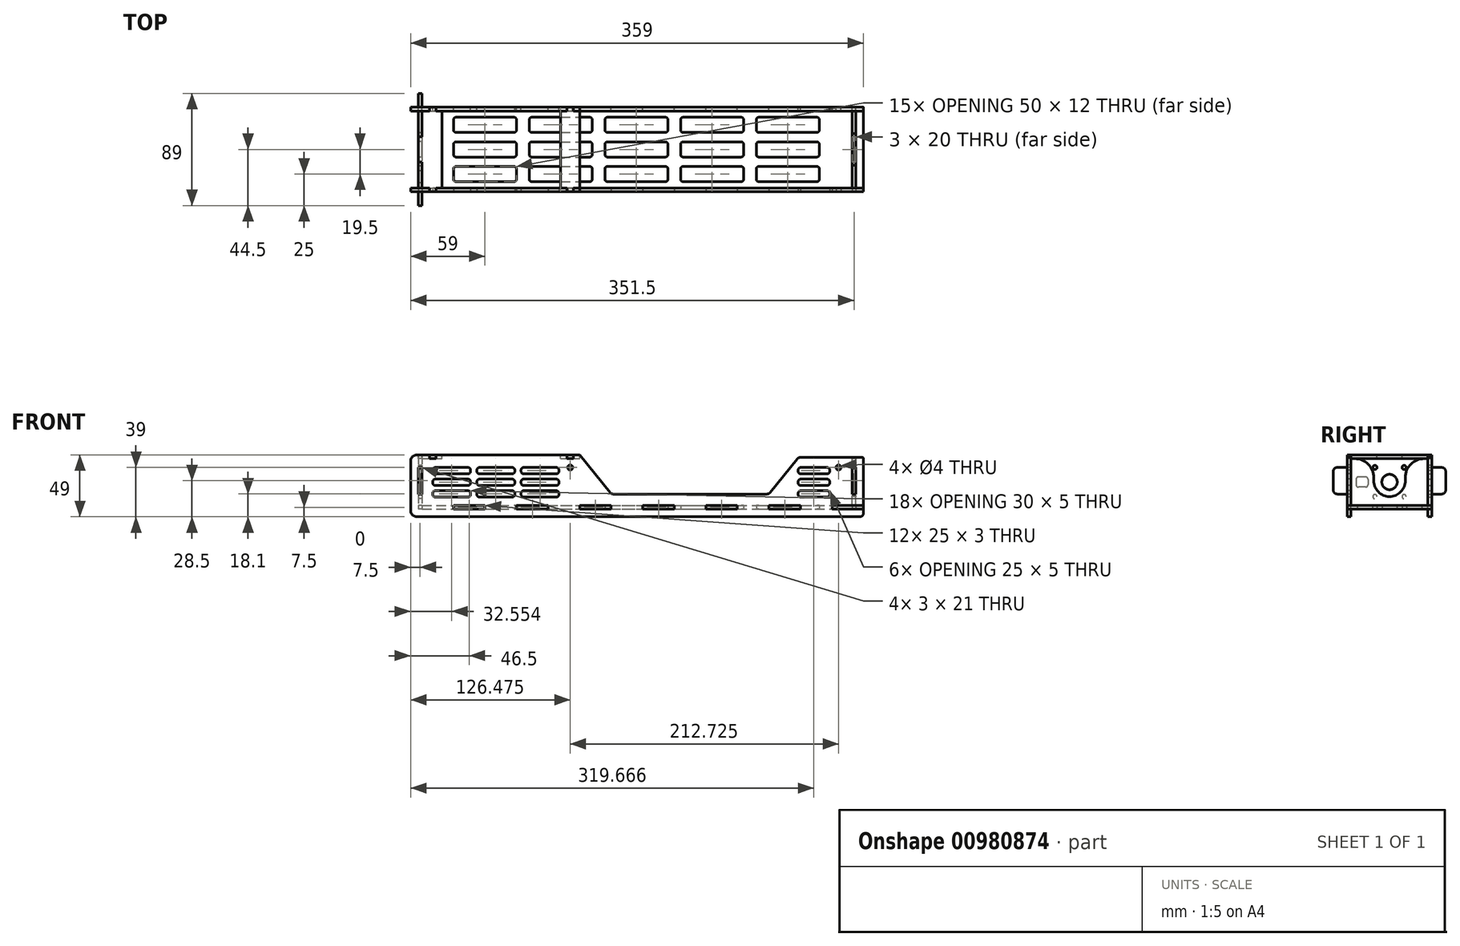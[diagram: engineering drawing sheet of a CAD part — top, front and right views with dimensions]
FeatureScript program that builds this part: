
annotation { "Feature Type Name" : "Feature", "Feature Type Description" : "" }
export const myFeature = defineFeature(function(context is Context, id is Id, definition is map)
    precondition{}
    {
        {
            assignVariable(context, id + "F0", {"variableType" : VariableType.LENGTH, "name" : "T", "lengthValue" : 3 * mm});
        }
        {
            var Q0;
            Q0=qCreatedBy(makeId("Top.planeOp"),FACE);
            var sketch = newSketch(context, id + "F1", { "sketchPlane" : qUnion([Q0])});
            skLineSegment(sketch, "E0", {"start": v(0, 0) * mm, "end": v(0, 33.5) * mm});
            skLineSegment(sketch, "E1", {"start": v(25, 33.5) * mm, "end": v(50, 33.5) * mm});
            skLineSegment(sketch, "E2", {"start": v(350, 33.5) * mm, "end": v(350, 0) * mm});
            skLineSegment(sketch, "E3", {"start": v(0, 30.5) * mm, "end": v(350, 30.5) * mm});
            skLineSegment(sketch, "E4", {"start": v(25, 33.5) * mm, "end": v(25, 30.5) * mm});
            skLineSegment(sketch, "E5.1.0.0", {"start": v(50, 33.5) * mm, "end": v(50, 30.5) * mm});
            skLineSegment(sketch, "E5.2.0.0", {"start": v(75, 33.5) * mm, "end": v(75, 30.5) * mm});
            skLineSegment(sketch, "E5.3.0.0", {"start": v(100, 33.5) * mm, "end": v(100, 30.5) * mm});
            skLineSegment(sketch, "E5.4.0.0", {"start": v(125, 33.5) * mm, "end": v(125, 30.5) * mm});
            skLineSegment(sketch, "E5.5.0.0", {"start": v(150, 33.5) * mm, "end": v(150, 30.5) * mm});
            skLineSegment(sketch, "E5.6.0.0", {"start": v(175, 33.5) * mm, "end": v(175, 30.5) * mm});
            skLineSegment(sketch, "E5.7.0.0", {"start": v(200, 33.5) * mm, "end": v(200, 30.5) * mm});
            skLineSegment(sketch, "E5.8.0.0", {"start": v(225, 33.5) * mm, "end": v(225, 30.5) * mm});
            skLineSegment(sketch, "E5.9.0.0", {"start": v(250, 33.5) * mm, "end": v(250, 30.5) * mm});
            skLineSegment(sketch, "E5.10.0.0", {"start": v(275, 33.5) * mm, "end": v(275, 30.5) * mm});
            skLineSegment(sketch, "E5.11.0.0", {"start": v(300, 33.5) * mm, "end": v(300, 30.5) * mm});
            skLineSegment(sketch, "E5.12.0.0", {"start": v(325, 33.5) * mm, "end": v(325, 30.5) * mm});
            skLineSegment(sketch, "E5.direction1", {"start": v(25, 30.5) * mm, "end": v(50, 30.5) * mm, "construction": true});
            skLineSegment(sketch, "E6.trimOffspring", {"start": v(75, 33.5) * mm, "end": v(100, 33.5) * mm});
            skLineSegment(sketch, "E7.trimOffspring", {"start": v(125, 33.5) * mm, "end": v(150, 33.5) * mm});
            skLineSegment(sketch, "E8.trimOffspring", {"start": v(175, 33.5) * mm, "end": v(200, 33.5) * mm});
            skLineSegment(sketch, "E9.trimOffspring", {"start": v(225, 33.5) * mm, "end": v(250, 33.5) * mm});
            skLineSegment(sketch, "E10.trimOffspring", {"start": v(275, 33.5) * mm, "end": v(300, 33.5) * mm});
            skLineSegment(sketch, "E11.trimOffspring", {"start": v(325, 33.5) * mm, "end": v(350, 33.5) * mm});
            skLineSegment(sketch, "E12", {"start": v(25, 0) * mm, "end": v(25, 4) * mm});
            skLineSegment(sketch, "E13", {"start": v(27, 6) * mm, "end": v(73, 6) * mm});
            skLineSegment(sketch, "E14", {"start": v(75, 4) * mm, "end": v(75, 0) * mm});
            skLineSegment(sketch, "E15", {"start": v(27, 25.5) * mm, "end": v(73, 25.5) * mm});
            skLineSegment(sketch, "E16", {"start": v(25, 23.5) * mm, "end": v(25, 15.5) * mm});
            skLineSegment(sketch, "E17", {"start": v(27, 13.5) * mm, "end": v(73, 13.5) * mm});
            skLineSegment(sketch, "E18", {"start": v(75, 15.5) * mm, "end": v(75, 23.5) * mm});
            skLineSegment(sketch, "E19.1.0.0", {"start": v(135, 15.5) * mm, "end": v(135, 23.5) * mm});
            skLineSegment(sketch, "E19.1.0.1", {"start": v(87, 13.5) * mm, "end": v(133, 13.5) * mm});
            skLineSegment(sketch, "E19.1.0.2", {"start": v(85, 23.5) * mm, "end": v(85, 15.5) * mm});
            skLineSegment(sketch, "E19.1.0.3", {"start": v(87, 25.5) * mm, "end": v(133, 25.5) * mm});
            skLineSegment(sketch, "E19.1.0.4", {"start": v(87, 6) * mm, "end": v(133, 6) * mm});
            skLineSegment(sketch, "E19.1.0.5", {"start": v(85, 0) * mm, "end": v(85, 4) * mm});
            skLineSegment(sketch, "E19.1.0.6", {"start": v(135, 4) * mm, "end": v(135, 0) * mm});
            skLineSegment(sketch, "E19.2.0.0", {"start": v(195, 15.5) * mm, "end": v(195, 23.5) * mm});
            skLineSegment(sketch, "E19.2.0.1", {"start": v(147, 13.5) * mm, "end": v(193, 13.5) * mm});
            skLineSegment(sketch, "E19.2.0.2", {"start": v(145, 23.5) * mm, "end": v(145, 15.5) * mm});
            skLineSegment(sketch, "E19.2.0.3", {"start": v(147, 25.5) * mm, "end": v(193, 25.5) * mm});
            skLineSegment(sketch, "E19.2.0.4", {"start": v(147, 6) * mm, "end": v(193, 6) * mm});
            skLineSegment(sketch, "E19.2.0.5", {"start": v(145, 0) * mm, "end": v(145, 4) * mm});
            skLineSegment(sketch, "E19.2.0.6", {"start": v(195, 4) * mm, "end": v(195, 0) * mm});
            skLineSegment(sketch, "E19.3.0.0", {"start": v(255, 15.5) * mm, "end": v(255, 23.5) * mm});
            skLineSegment(sketch, "E19.3.0.1", {"start": v(207, 13.5) * mm, "end": v(253, 13.5) * mm});
            skLineSegment(sketch, "E19.3.0.2", {"start": v(205, 23.5) * mm, "end": v(205, 15.5) * mm});
            skLineSegment(sketch, "E19.3.0.3", {"start": v(207, 25.5) * mm, "end": v(253, 25.5) * mm});
            skLineSegment(sketch, "E19.3.0.4", {"start": v(207, 6) * mm, "end": v(253, 6) * mm});
            skLineSegment(sketch, "E19.3.0.5", {"start": v(205, 0) * mm, "end": v(205, 4) * mm});
            skLineSegment(sketch, "E19.3.0.6", {"start": v(255, 4) * mm, "end": v(255, 0) * mm});
            skLineSegment(sketch, "E19.4.0.0", {"start": v(315, 15.5) * mm, "end": v(315, 23.5) * mm});
            skLineSegment(sketch, "E19.4.0.1", {"start": v(267, 13.5) * mm, "end": v(313, 13.5) * mm});
            skLineSegment(sketch, "E19.4.0.2", {"start": v(265, 23.5) * mm, "end": v(265, 15.5) * mm});
            skLineSegment(sketch, "E19.4.0.3", {"start": v(267, 25.5) * mm, "end": v(313, 25.5) * mm});
            skLineSegment(sketch, "E19.4.0.4", {"start": v(267, 6) * mm, "end": v(313, 6) * mm});
            skLineSegment(sketch, "E19.4.0.5", {"start": v(265, 0) * mm, "end": v(265, 4) * mm});
            skLineSegment(sketch, "E19.4.0.6", {"start": v(315, 4) * mm, "end": v(315, 0) * mm});
            skLineSegment(sketch, "E19.direction1", {"start": v(25, 0) * mm, "end": v(85, 0) * mm, "construction": true});
            skLineSegment(sketch, "E20.MirrorCS", {"start": v(275, -33.5) * mm, "end": v(275, -30.5) * mm});
            skLineSegment(sketch, "E21.MirrorCS", {"start": v(250, -33.5) * mm, "end": v(250, -30.5) * mm});
            skLineSegment(sketch, "E22.MirrorCS", {"start": v(300, -33.5) * mm, "end": v(300, -30.5) * mm});
            skLineSegment(sketch, "E23.MirrorCS", {"start": v(225, -33.5) * mm, "end": v(225, -30.5) * mm});
            skLineSegment(sketch, "E24.MirrorCS", {"start": v(200, -33.5) * mm, "end": v(200, -30.5) * mm});
            skLineSegment(sketch, "E25.MirrorCS", {"start": v(325, -33.5) * mm, "end": v(325, -30.5) * mm});
            skLineSegment(sketch, "E26.MirrorCS", {"start": v(175, -33.5) * mm, "end": v(175, -30.5) * mm});
            skLineSegment(sketch, "E27.MirrorCS", {"start": v(85, -23.5) * mm, "end": v(85, -15.5) * mm});
            skLineSegment(sketch, "E28.MirrorCS", {"start": v(150, -33.5) * mm, "end": v(150, -30.5) * mm});
            skLineSegment(sketch, "E29.MirrorCS", {"start": v(125, -33.5) * mm, "end": v(125, -30.5) * mm});
            skLineSegment(sketch, "E30.MirrorCS", {"start": v(135, -15.5) * mm, "end": v(135, -23.5) * mm});
            skLineSegment(sketch, "E31.MirrorCS", {"start": v(205, -23.5) * mm, "end": v(205, -15.5) * mm});
            skLineSegment(sketch, "E32.MirrorCS", {"start": v(100, -33.5) * mm, "end": v(100, -30.5) * mm});
            skLineSegment(sketch, "E33.MirrorCS", {"start": v(85, 0) * mm, "end": v(85, -4) * mm});
            skLineSegment(sketch, "E34.MirrorCS", {"start": v(50, -33.5) * mm, "end": v(50, -30.5) * mm});
            skLineSegment(sketch, "E35.MirrorCS", {"start": v(255, -15.5) * mm, "end": v(255, -23.5) * mm});
            skLineSegment(sketch, "E36.MirrorCS", {"start": v(25, -33.5) * mm, "end": v(25, -30.5) * mm});
            skLineSegment(sketch, "E37.MirrorCS", {"start": v(265, -23.5) * mm, "end": v(265, -15.5) * mm});
            skLineSegment(sketch, "E38.MirrorCS", {"start": v(25, 0) * mm, "end": v(25, -4) * mm});
            skLineSegment(sketch, "E39.MirrorCS", {"start": v(195, -15.5) * mm, "end": v(195, -23.5) * mm});
            skLineSegment(sketch, "E40.MirrorCS", {"start": v(75, -15.5) * mm, "end": v(75, -23.5) * mm});
            skLineSegment(sketch, "E41.MirrorCS", {"start": v(25, -23.5) * mm, "end": v(25, -15.5) * mm});
            skLineSegment(sketch, "E42.MirrorCS", {"start": v(315, -15.5) * mm, "end": v(315, -23.5) * mm});
            skLineSegment(sketch, "E43.MirrorCS", {"start": v(75, -33.5) * mm, "end": v(75, -30.5) * mm});
            skLineSegment(sketch, "E44.MirrorCS", {"start": v(145, -23.5) * mm, "end": v(145, -15.5) * mm});
            skLineSegment(sketch, "E45.MirrorCS", {"start": v(205, 0) * mm, "end": v(205, -4) * mm});
            skLineSegment(sketch, "E46.MirrorCS", {"start": v(255, -4) * mm, "end": v(255, 0) * mm});
            skLineSegment(sketch, "E47.MirrorCS", {"start": v(315, -4) * mm, "end": v(315, 0) * mm});
            skLineSegment(sketch, "E48.MirrorCS", {"start": v(195, -4) * mm, "end": v(195, 0) * mm});
            skLineSegment(sketch, "E49.MirrorCS", {"start": v(135, -4) * mm, "end": v(135, 0) * mm});
            skLineSegment(sketch, "E50.MirrorCS", {"start": v(75, -4) * mm, "end": v(75, 0) * mm});
            skLineSegment(sketch, "E51.MirrorCS", {"start": v(265, 0) * mm, "end": v(265, -4) * mm});
            skLineSegment(sketch, "E52.MirrorCS", {"start": v(145, 0) * mm, "end": v(145, -4) * mm});
            skLineSegment(sketch, "E53.MirrorCS", {"start": v(87, -13.5) * mm, "end": v(133, -13.5) * mm});
            skLineSegment(sketch, "E54.MirrorCS", {"start": v(207, -25.5) * mm, "end": v(253, -25.5) * mm});
            skLineSegment(sketch, "E55.MirrorCS", {"start": v(25, -30.5) * mm, "end": v(50, -30.5) * mm, "construction": true});
            skLineSegment(sketch, "E56.MirrorCS", {"start": v(207, -6) * mm, "end": v(253, -6) * mm});
            skLineSegment(sketch, "E57.MirrorCS", {"start": v(75, -33.5) * mm, "end": v(100, -33.5) * mm});
            skLineSegment(sketch, "E58.MirrorCS", {"start": v(87, -25.5) * mm, "end": v(133, -25.5) * mm});
            skLineSegment(sketch, "E59.MirrorCS", {"start": v(125, -33.5) * mm, "end": v(150, -33.5) * mm});
            skLineSegment(sketch, "E60.MirrorCS", {"start": v(87, -6) * mm, "end": v(133, -6) * mm});
            skLineSegment(sketch, "E61.MirrorCS", {"start": v(175, -33.5) * mm, "end": v(200, -33.5) * mm});
            skLineSegment(sketch, "E62.MirrorCS", {"start": v(27, -13.5) * mm, "end": v(73, -13.5) * mm});
            skLineSegment(sketch, "E63.MirrorCS", {"start": v(147, -25.5) * mm, "end": v(193, -25.5) * mm});
            skLineSegment(sketch, "E64.MirrorCS", {"start": v(0, 0) * mm, "end": v(0, -33.5) * mm});
            skLineSegment(sketch, "E65.MirrorCS", {"start": v(225, -33.5) * mm, "end": v(250, -33.5) * mm});
            skLineSegment(sketch, "E66.MirrorCS", {"start": v(147, -13.5) * mm, "end": v(193, -13.5) * mm});
            skLineSegment(sketch, "E67.MirrorCS", {"start": v(350, -33.5) * mm, "end": v(350, 0) * mm});
            skLineSegment(sketch, "E68.MirrorCS", {"start": v(27, -6) * mm, "end": v(73, -6) * mm});
            skLineSegment(sketch, "E69.MirrorCS", {"start": v(267, -6) * mm, "end": v(313, -6) * mm});
            skLineSegment(sketch, "E70.MirrorCS", {"start": v(325, -33.5) * mm, "end": v(350, -33.5) * mm});
            skLineSegment(sketch, "E71.MirrorCS", {"start": v(25, -33.5) * mm, "end": v(50, -33.5) * mm});
            skLineSegment(sketch, "E72.MirrorCS", {"start": v(147, -6) * mm, "end": v(193, -6) * mm});
            skLineSegment(sketch, "E73.MirrorCS", {"start": v(0, -30.5) * mm, "end": v(350, -30.5) * mm});
            skLineSegment(sketch, "E74.MirrorCS", {"start": v(27, -25.5) * mm, "end": v(73, -25.5) * mm});
            skLineSegment(sketch, "E75.MirrorCS", {"start": v(207, -13.5) * mm, "end": v(253, -13.5) * mm});
            skLineSegment(sketch, "E76.MirrorCS", {"start": v(275, -33.5) * mm, "end": v(300, -33.5) * mm});
            skLineSegment(sketch, "E77.MirrorCS", {"start": v(267, -25.5) * mm, "end": v(313, -25.5) * mm});
            skLineSegment(sketch, "E78.MirrorCS", {"start": v(267, -13.5) * mm, "end": v(313, -13.5) * mm});
            skLineSegment(sketch, "E79", {"start": v(0, 10) * mm, "end": v(-3, 10) * mm});
            skLineSegment(sketch, "E80", {"start": v(-3, 10) * mm, "end": v(-3, 0) * mm});
            skLineSegment(sketch, "E81.MirrorCS", {"start": v(-3, -10) * mm, "end": v(-3, 0) * mm});
            skLineSegment(sketch, "E82.MirrorCS", {"start": v(0, -10) * mm, "end": v(-3, -10) * mm});
            skLineSegment(sketch, "E83", {"start": v(350, 0) * mm, "end": v(344, 0) * mm, "construction": true});
            skLineSegment(sketch, "E84", {"start": v(344, 0) * mm, "end": v(344, 10) * mm});
            skLineSegment(sketch, "E85", {"start": v(344, 10) * mm, "end": v(341, 10) * mm});
            skLineSegment(sketch, "E86", {"start": v(341, 10) * mm, "end": v(341, -10) * mm});
            skLineSegment(sketch, "E87", {"start": v(341, -10) * mm, "end": v(344, -10) * mm});
            skLineSegment(sketch, "E88", {"start": v(344, -10) * mm, "end": v(344, 0) * mm});
            skPoint(sketch, "E89.visualSharp", {"position": v(25, 25.5) * mm});
            skArc(sketch, "E89.filletArc", {"start": v(27, 25.5) * mm, "mid": v(25.59, 24.91) * mm, "end": v(25, 23.5) * mm});
            skPoint(sketch, "E90.visualSharp", {"position": v(25, 13.5) * mm});
            skArc(sketch, "E90.filletArc", {"start": v(25, 15.5) * mm, "mid": v(25.59, 14.09) * mm, "end": v(27, 13.5) * mm});
            skPoint(sketch, "E91.visualSharp", {"position": v(75, 13.5) * mm});
            skArc(sketch, "E91.filletArc", {"start": v(73, 13.5) * mm, "mid": v(74.41, 14.09) * mm, "end": v(75, 15.5) * mm});
            skPoint(sketch, "E92.visualSharp", {"position": v(75, 25.5) * mm});
            skArc(sketch, "E92.filletArc", {"start": v(75, 23.5) * mm, "mid": v(74.41, 24.91) * mm, "end": v(73, 25.5) * mm});
            skPoint(sketch, "E93.visualSharp", {"position": v(75, 6) * mm});
            skArc(sketch, "E93.filletArc", {"start": v(75, 4) * mm, "mid": v(74.41, 5.41) * mm, "end": v(73, 6) * mm});
            skPoint(sketch, "E94.visualSharp", {"position": v(25, 6) * mm});
            skArc(sketch, "E94.filletArc", {"start": v(27, 6) * mm, "mid": v(25.59, 5.41) * mm, "end": v(25, 4) * mm});
            skPoint(sketch, "E95.visualSharp", {"position": v(25, -6) * mm});
            skArc(sketch, "E95.filletArc", {"start": v(25, -4) * mm, "mid": v(25.59, -5.41) * mm, "end": v(27, -6) * mm});
            skPoint(sketch, "E96.visualSharp", {"position": v(75, -6) * mm});
            skArc(sketch, "E96.filletArc", {"start": v(73, -6) * mm, "mid": v(74.41, -5.41) * mm, "end": v(75, -4) * mm});
            skPoint(sketch, "E97.visualSharp", {"position": v(85, 25.5) * mm});
            skArc(sketch, "E97.filletArc", {"start": v(87, 25.5) * mm, "mid": v(85.59, 24.91) * mm, "end": v(85, 23.5) * mm});
            skPoint(sketch, "E98.visualSharp", {"position": v(135, 13.5) * mm});
            skArc(sketch, "E98.filletArc", {"start": v(133, 13.5) * mm, "mid": v(134.41, 14.09) * mm, "end": v(135, 15.5) * mm});
            skPoint(sketch, "E99.visualSharp", {"position": v(135, 25.5) * mm});
            skArc(sketch, "E99.filletArc", {"start": v(135, 23.5) * mm, "mid": v(134.41, 24.91) * mm, "end": v(133, 25.5) * mm});
            skPoint(sketch, "E100.visualSharp", {"position": v(85, 13.5) * mm});
            skArc(sketch, "E100.filletArc", {"start": v(85, 15.5) * mm, "mid": v(85.59, 14.09) * mm, "end": v(87, 13.5) * mm});
            skPoint(sketch, "E101.visualSharp", {"position": v(85, 6) * mm});
            skArc(sketch, "E101.filletArc", {"start": v(87, 6) * mm, "mid": v(85.59, 5.41) * mm, "end": v(85, 4) * mm});
            skPoint(sketch, "E102.visualSharp", {"position": v(135, -6) * mm});
            skArc(sketch, "E102.filletArc", {"start": v(133, -6) * mm, "mid": v(134.41, -5.41) * mm, "end": v(135, -4) * mm});
            skPoint(sketch, "E103.visualSharp", {"position": v(85, -6) * mm});
            skArc(sketch, "E103.filletArc", {"start": v(85, -4) * mm, "mid": v(85.59, -5.41) * mm, "end": v(87, -6) * mm});
            skPoint(sketch, "E104.visualSharp", {"position": v(135, 6) * mm});
            skArc(sketch, "E104.filletArc", {"start": v(135, 4) * mm, "mid": v(134.41, 5.41) * mm, "end": v(133, 6) * mm});
            skPoint(sketch, "E105.visualSharp", {"position": v(145, 13.5) * mm});
            skArc(sketch, "E105.filletArc", {"start": v(145, 15.5) * mm, "mid": v(145.59, 14.09) * mm, "end": v(147, 13.5) * mm});
            skPoint(sketch, "E106.visualSharp", {"position": v(145, 25.5) * mm});
            skArc(sketch, "E106.filletArc", {"start": v(147, 25.5) * mm, "mid": v(145.59, 24.91) * mm, "end": v(145, 23.5) * mm});
            skPoint(sketch, "E107.visualSharp", {"position": v(195, 25.5) * mm});
            skArc(sketch, "E107.filletArc", {"start": v(195, 23.5) * mm, "mid": v(194.41, 24.91) * mm, "end": v(193, 25.5) * mm});
            skPoint(sketch, "E108.visualSharp", {"position": v(195, 6) * mm});
            skArc(sketch, "E108.filletArc", {"start": v(195, 4) * mm, "mid": v(194.41, 5.41) * mm, "end": v(193, 6) * mm});
            skPoint(sketch, "E109.visualSharp", {"position": v(195, 13.5) * mm});
            skArc(sketch, "E109.filletArc", {"start": v(193, 13.5) * mm, "mid": v(194.41, 14.09) * mm, "end": v(195, 15.5) * mm});
            skPoint(sketch, "E110.visualSharp", {"position": v(145, -6) * mm});
            skArc(sketch, "E110.filletArc", {"start": v(145, -4) * mm, "mid": v(145.59, -5.41) * mm, "end": v(147, -6) * mm});
            skPoint(sketch, "E111.visualSharp", {"position": v(145, 6) * mm});
            skArc(sketch, "E111.filletArc", {"start": v(147, 6) * mm, "mid": v(145.59, 5.41) * mm, "end": v(145, 4) * mm});
            skPoint(sketch, "E112.visualSharp", {"position": v(195, -6) * mm});
            skArc(sketch, "E112.filletArc", {"start": v(193, -6) * mm, "mid": v(194.41, -5.41) * mm, "end": v(195, -4) * mm});
            skPoint(sketch, "E113.visualSharp", {"position": v(25, -13.5) * mm});
            skArc(sketch, "E113.filletArc", {"start": v(27, -13.5) * mm, "mid": v(25.59, -14.09) * mm, "end": v(25, -15.5) * mm});
            skPoint(sketch, "E114.visualSharp", {"position": v(75, -25.5) * mm});
            skArc(sketch, "E114.filletArc", {"start": v(73, -25.5) * mm, "mid": v(74.41, -24.91) * mm, "end": v(75, -23.5) * mm});
            skPoint(sketch, "E115.visualSharp", {"position": v(75, -13.5) * mm});
            skArc(sketch, "E115.filletArc", {"start": v(75, -15.5) * mm, "mid": v(74.41, -14.09) * mm, "end": v(73, -13.5) * mm});
            skPoint(sketch, "E116.visualSharp", {"position": v(25, -25.5) * mm});
            skArc(sketch, "E116.filletArc", {"start": v(25, -23.5) * mm, "mid": v(25.59, -24.91) * mm, "end": v(27, -25.5) * mm});
            skPoint(sketch, "E117.visualSharp", {"position": v(85, -25.5) * mm});
            skArc(sketch, "E117.filletArc", {"start": v(85, -23.5) * mm, "mid": v(85.59, -24.91) * mm, "end": v(87, -25.5) * mm});
            skPoint(sketch, "E118.visualSharp", {"position": v(85, -13.5) * mm});
            skArc(sketch, "E118.filletArc", {"start": v(87, -13.5) * mm, "mid": v(85.59, -14.09) * mm, "end": v(85, -15.5) * mm});
            skPoint(sketch, "E119.visualSharp", {"position": v(135, -13.5) * mm});
            skArc(sketch, "E119.filletArc", {"start": v(135, -15.5) * mm, "mid": v(134.41, -14.09) * mm, "end": v(133, -13.5) * mm});
            skPoint(sketch, "E120.visualSharp", {"position": v(135, -25.5) * mm});
            skArc(sketch, "E120.filletArc", {"start": v(133, -25.5) * mm, "mid": v(134.41, -24.91) * mm, "end": v(135, -23.5) * mm});
            skPoint(sketch, "E121.visualSharp", {"position": v(145, -13.5) * mm});
            skArc(sketch, "E121.filletArc", {"start": v(147, -13.5) * mm, "mid": v(145.59, -14.09) * mm, "end": v(145, -15.5) * mm});
            skPoint(sketch, "E122.visualSharp", {"position": v(145, -25.5) * mm});
            skArc(sketch, "E122.filletArc", {"start": v(145, -23.5) * mm, "mid": v(145.59, -24.91) * mm, "end": v(147, -25.5) * mm});
            skPoint(sketch, "E123.visualSharp", {"position": v(195, -25.5) * mm});
            skArc(sketch, "E123.filletArc", {"start": v(193, -25.5) * mm, "mid": v(194.41, -24.91) * mm, "end": v(195, -23.5) * mm});
            skPoint(sketch, "E124.visualSharp", {"position": v(195, -13.5) * mm});
            skArc(sketch, "E124.filletArc", {"start": v(195, -15.5) * mm, "mid": v(194.41, -14.09) * mm, "end": v(193, -13.5) * mm});
            skPoint(sketch, "E125.visualSharp", {"position": v(205, -25.5) * mm});
            skArc(sketch, "E125.filletArc", {"start": v(205, -23.5) * mm, "mid": v(205.59, -24.91) * mm, "end": v(207, -25.5) * mm});
            skPoint(sketch, "E126.visualSharp", {"position": v(205, -13.5) * mm});
            skArc(sketch, "E126.filletArc", {"start": v(207, -13.5) * mm, "mid": v(205.59, -14.09) * mm, "end": v(205, -15.5) * mm});
            skPoint(sketch, "E127.visualSharp", {"position": v(205, -6) * mm});
            skArc(sketch, "E127.filletArc", {"start": v(205, -4) * mm, "mid": v(205.59, -5.41) * mm, "end": v(207, -6) * mm});
            skPoint(sketch, "E128.visualSharp", {"position": v(205, 6) * mm});
            skArc(sketch, "E128.filletArc", {"start": v(207, 6) * mm, "mid": v(205.59, 5.41) * mm, "end": v(205, 4) * mm});
            skPoint(sketch, "E129.visualSharp", {"position": v(205, 25.5) * mm});
            skArc(sketch, "E129.filletArc", {"start": v(207, 25.5) * mm, "mid": v(205.59, 24.91) * mm, "end": v(205, 23.5) * mm});
            skPoint(sketch, "E130.visualSharp", {"position": v(205, 13.5) * mm});
            skArc(sketch, "E130.filletArc", {"start": v(205, 15.5) * mm, "mid": v(205.59, 14.09) * mm, "end": v(207, 13.5) * mm});
            skPoint(sketch, "E131.visualSharp", {"position": v(255, 25.5) * mm});
            skArc(sketch, "E131.filletArc", {"start": v(255, 23.5) * mm, "mid": v(254.41, 24.91) * mm, "end": v(253, 25.5) * mm});
            skPoint(sketch, "E132.visualSharp", {"position": v(255, 13.5) * mm});
            skArc(sketch, "E132.filletArc", {"start": v(253, 13.5) * mm, "mid": v(254.41, 14.09) * mm, "end": v(255, 15.5) * mm});
            skPoint(sketch, "E133.visualSharp", {"position": v(255, 6) * mm});
            skArc(sketch, "E133.filletArc", {"start": v(255, 4) * mm, "mid": v(254.41, 5.41) * mm, "end": v(253, 6) * mm});
            skPoint(sketch, "E134.visualSharp", {"position": v(255, -6) * mm});
            skArc(sketch, "E134.filletArc", {"start": v(253, -6) * mm, "mid": v(254.41, -5.41) * mm, "end": v(255, -4) * mm});
            skPoint(sketch, "E135.visualSharp", {"position": v(255, -25.5) * mm});
            skArc(sketch, "E135.filletArc", {"start": v(253, -25.5) * mm, "mid": v(254.41, -24.91) * mm, "end": v(255, -23.5) * mm});
            skPoint(sketch, "E136.visualSharp", {"position": v(255, -13.5) * mm});
            skArc(sketch, "E136.filletArc", {"start": v(255, -15.5) * mm, "mid": v(254.41, -14.09) * mm, "end": v(253, -13.5) * mm});
            skPoint(sketch, "E137.visualSharp", {"position": v(265, -25.5) * mm});
            skArc(sketch, "E137.filletArc", {"start": v(265, -23.5) * mm, "mid": v(265.59, -24.91) * mm, "end": v(267, -25.5) * mm});
            skPoint(sketch, "E138.visualSharp", {"position": v(265, -13.5) * mm});
            skArc(sketch, "E138.filletArc", {"start": v(267, -13.5) * mm, "mid": v(265.59, -14.09) * mm, "end": v(265, -15.5) * mm});
            skPoint(sketch, "E139.visualSharp", {"position": v(265, -6) * mm});
            skArc(sketch, "E139.filletArc", {"start": v(265, -4) * mm, "mid": v(265.59, -5.41) * mm, "end": v(267, -6) * mm});
            skPoint(sketch, "E140.visualSharp", {"position": v(265, 6) * mm});
            skArc(sketch, "E140.filletArc", {"start": v(267, 6) * mm, "mid": v(265.59, 5.41) * mm, "end": v(265, 4) * mm});
            skPoint(sketch, "E141.visualSharp", {"position": v(265, 13.5) * mm});
            skArc(sketch, "E141.filletArc", {"start": v(265, 15.5) * mm, "mid": v(265.59, 14.09) * mm, "end": v(267, 13.5) * mm});
            skPoint(sketch, "E142.visualSharp", {"position": v(265, 25.5) * mm});
            skArc(sketch, "E142.filletArc", {"start": v(267, 25.5) * mm, "mid": v(265.59, 24.91) * mm, "end": v(265, 23.5) * mm});
            skPoint(sketch, "E143.visualSharp", {"position": v(315, 25.5) * mm});
            skArc(sketch, "E143.filletArc", {"start": v(315, 23.5) * mm, "mid": v(314.41, 24.91) * mm, "end": v(313, 25.5) * mm});
            skPoint(sketch, "E144.visualSharp", {"position": v(315, 13.5) * mm});
            skArc(sketch, "E144.filletArc", {"start": v(313, 13.5) * mm, "mid": v(314.41, 14.09) * mm, "end": v(315, 15.5) * mm});
            skPoint(sketch, "E145.visualSharp", {"position": v(315, -6) * mm});
            skArc(sketch, "E145.filletArc", {"start": v(313, -6) * mm, "mid": v(314.41, -5.41) * mm, "end": v(315, -4) * mm});
            skPoint(sketch, "E146.visualSharp", {"position": v(315, 6) * mm});
            skArc(sketch, "E146.filletArc", {"start": v(315, 4) * mm, "mid": v(314.41, 5.41) * mm, "end": v(313, 6) * mm});
            skPoint(sketch, "E147.visualSharp", {"position": v(315, -13.5) * mm});
            skArc(sketch, "E147.filletArc", {"start": v(315, -15.5) * mm, "mid": v(314.41, -14.09) * mm, "end": v(313, -13.5) * mm});
            skPoint(sketch, "E148.visualSharp", {"position": v(315, -25.5) * mm});
            skArc(sketch, "E148.filletArc", {"start": v(313, -25.5) * mm, "mid": v(314.41, -24.91) * mm, "end": v(315, -23.5) * mm});
            skSolve(sketch);
        }
        {
            var Q0;
            Q0=makeQuery(id+"F1.imprint","IMPRINT",FACE,{"disambiguationData":[TD([[makeQuery(id+"F1.imprint","IMPRINT",EDGE,{"derivedFrom":sQuery(id+"F1.wireOp",EDGE,"E12")}),1.0]])]});
            var Q1;
            Q1=makeQuery(id+"F1.imprint","IMPRINT",FACE,{"disambiguationData":[TD([[makeQuery(id+"F1.imprint","IMPRINT",EDGE,{"derivedFrom":sQuery(id+"F1.wireOp",EDGE,"E1")}),-1.0]])]});
            var Q2;
            {var subQ0=sQuery(id+"F1.wireOp",EDGE,"E5.2.0.0");Q2=makeQuery(id+"F1.imprint","IMPRINT",FACE,{"disambiguationData":[TD([[makeQuery(id+"F1.imprint","IMPRINT",EDGE,{"derivedFrom":subQ0}),1.0]])]});}
            var Q3;
            {var subQ0=sQuery(id+"F1.wireOp",EDGE,"E5.4.0.0");Q3=makeQuery(id+"F1.imprint","IMPRINT",FACE,{"disambiguationData":[TD([[makeQuery(id+"F1.imprint","IMPRINT",EDGE,{"derivedFrom":subQ0}),1.0]])]});}
            var Q4;
            {var subQ0=sQuery(id+"F1.wireOp",EDGE,"E5.6.0.0");Q4=makeQuery(id+"F1.imprint","IMPRINT",FACE,{"disambiguationData":[TD([[makeQuery(id+"F1.imprint","IMPRINT",EDGE,{"derivedFrom":subQ0}),1.0]])]});}
            var Q5;
            {var subQ0=sQuery(id+"F1.wireOp",EDGE,"E5.8.0.0");Q5=makeQuery(id+"F1.imprint","IMPRINT",FACE,{"disambiguationData":[TD([[makeQuery(id+"F1.imprint","IMPRINT",EDGE,{"derivedFrom":subQ0}),1.0]])]});}
            var Q6;
            {var subQ0=sQuery(id+"F1.wireOp",EDGE,"E34.MirrorCS");Q6=makeQuery(id+"F1.imprint","IMPRINT",FACE,{"disambiguationData":[TD([[makeQuery(id+"F1.imprint","IMPRINT",EDGE,{"derivedFrom":subQ0}),1.0]])]});}
            var Q7;
            {var subQ0=sQuery(id+"F1.wireOp",EDGE,"E32.MirrorCS");Q7=makeQuery(id+"F1.imprint","IMPRINT",FACE,{"disambiguationData":[TD([[makeQuery(id+"F1.imprint","IMPRINT",EDGE,{"derivedFrom":subQ0}),1.0]])]});}
            var Q8;
            {var subQ0=sQuery(id+"F1.wireOp",EDGE,"E28.MirrorCS");Q8=makeQuery(id+"F1.imprint","IMPRINT",FACE,{"disambiguationData":[TD([[makeQuery(id+"F1.imprint","IMPRINT",EDGE,{"derivedFrom":subQ0}),1.0]])]});}
            var Q9;
            {var subQ0=sQuery(id+"F1.wireOp",EDGE,"E24.MirrorCS");Q9=makeQuery(id+"F1.imprint","IMPRINT",FACE,{"disambiguationData":[TD([[makeQuery(id+"F1.imprint","IMPRINT",EDGE,{"derivedFrom":subQ0}),1.0]])]});}
            var Q10;
            {var subQ0=sQuery(id+"F1.wireOp",EDGE,"E21.MirrorCS");Q10=makeQuery(id+"F1.imprint","IMPRINT",FACE,{"disambiguationData":[TD([[makeQuery(id+"F1.imprint","IMPRINT",EDGE,{"derivedFrom":subQ0}),1.0]])]});}
            var Q11;
            {var subQ0=sQuery(id+"F1.wireOp",EDGE,"E5.10.0.0");Q11=makeQuery(id+"F1.imprint","IMPRINT",FACE,{"disambiguationData":[TD([[makeQuery(id+"F1.imprint","IMPRINT",EDGE,{"derivedFrom":subQ0}),1.0]])]});}
            var Q12;
            {var subQ4=sQuery(id+"F1.wireOp",EDGE,"E5.12.0.0");Q12=makeQuery(id+"F1.imprint","IMPRINT",FACE,{"disambiguationData":[TD([[makeQuery(id+"F1.imprint","IMPRINT",EDGE,{"derivedFrom":subQ4}),1.0]])]});}
            var Q13;
            {var subQ0=sQuery(id+"F1.wireOp",EDGE,"E20.MirrorCS");Q13=makeQuery(id+"F1.imprint","IMPRINT",FACE,{"disambiguationData":[TD([[makeQuery(id+"F1.imprint","IMPRINT",EDGE,{"derivedFrom":subQ0}),-1.0]])]});}
            var Q14;
            {var subQ0=sQuery(id+"F1.wireOp",EDGE,"E25.MirrorCS");Q14=makeQuery(id+"F1.imprint","IMPRINT",FACE,{"disambiguationData":[TD([[makeQuery(id+"F1.imprint","IMPRINT",EDGE,{"derivedFrom":subQ0}),-1.0]])]});}
            var Q15;
            {var subQ0=sQuery(id+"F1.wireOp",EDGE,"E79");Q15=makeQuery(id+"F1.imprint","IMPRINT",FACE,{"disambiguationData":[TD([[makeQuery(id+"F1.imprint","IMPRINT",EDGE,{"derivedFrom":subQ0}),1.0]])]});}
            extrude(context, id + "F2", {"entities" : qUnion([Q0, Q1, Q2, Q3, Q4, Q5, Q6, Q7, Q8, Q9, Q10, Q11, Q12, Q13, Q14, Q15]), "depth" : getVariable(context, 'T'), "offsetDistance" : 25 * mm});
        }
        {
            var Q0;
            Q0=makeQuery(id+"F2.opExtrude","SWEPT_FACE",FACE,{"disambiguationData":[OSD([sQuery(id+"F1.wireOp",EDGE,"E71.MirrorCS")])]});
            var sketch = newSketch(context, id + "F3", { "sketchPlane" : qUnion([Q0])});
            skLineSegment(sketch, "E149.0.1", {"start": v(25, 0) * mm, "end": v(25, 3) * mm});
            skLineSegment(sketch, "E149.0.3", {"start": v(0, 3) * mm, "end": v(0, 0) * mm});
            skLineSegment(sketch, "E150.0.0", {"start": v(25, 0) * mm, "end": v(50, 0) * mm});
            skLineSegment(sketch, "E150.0.1", {"start": v(50, 0) * mm, "end": v(50, 3) * mm});
            skLineSegment(sketch, "E150.0.2", {"start": v(50, 3) * mm, "end": v(25, 3) * mm});
            skLineSegment(sketch, "E150.0.3", {"start": v(25, 3) * mm, "end": v(25, 0) * mm});
            skLineSegment(sketch, "E151.0.1", {"start": v(75, 0) * mm, "end": v(75, 3) * mm});
            skLineSegment(sketch, "E151.0.3", {"start": v(50, 3) * mm, "end": v(50, 0) * mm});
            skLineSegment(sketch, "E152.0.0", {"start": v(75, 0) * mm, "end": v(100, 0) * mm});
            skLineSegment(sketch, "E152.0.1", {"start": v(100, 0) * mm, "end": v(100, 3) * mm});
            skLineSegment(sketch, "E152.0.2", {"start": v(100, 3) * mm, "end": v(75, 3) * mm});
            skLineSegment(sketch, "E152.0.3", {"start": v(75, 3) * mm, "end": v(75, 0) * mm});
            skLineSegment(sketch, "E153.0.1", {"start": v(125, 0) * mm, "end": v(125, 3) * mm});
            skLineSegment(sketch, "E153.0.3", {"start": v(100, 3) * mm, "end": v(100, 0) * mm});
            skLineSegment(sketch, "E154.0.0", {"start": v(125, 0) * mm, "end": v(150, 0) * mm});
            skLineSegment(sketch, "E154.0.1", {"start": v(150, 0) * mm, "end": v(150, 3) * mm});
            skLineSegment(sketch, "E154.0.2", {"start": v(150, 3) * mm, "end": v(125, 3) * mm});
            skLineSegment(sketch, "E154.0.3", {"start": v(125, 3) * mm, "end": v(125, 0) * mm});
            skLineSegment(sketch, "E155.0.1", {"start": v(175, 0) * mm, "end": v(175, 3) * mm});
            skLineSegment(sketch, "E155.0.3", {"start": v(150, 3) * mm, "end": v(150, 0) * mm});
            skLineSegment(sketch, "E156.0.0", {"start": v(175, 0) * mm, "end": v(200, 0) * mm});
            skLineSegment(sketch, "E156.0.1", {"start": v(200, 0) * mm, "end": v(200, 3) * mm});
            skLineSegment(sketch, "E156.0.2", {"start": v(200, 3) * mm, "end": v(175, 3) * mm});
            skLineSegment(sketch, "E156.0.3", {"start": v(175, 3) * mm, "end": v(175, 0) * mm});
            skLineSegment(sketch, "E157.0.1", {"start": v(225, 0) * mm, "end": v(225, 3) * mm});
            skLineSegment(sketch, "E157.0.3", {"start": v(200, 3) * mm, "end": v(200, 0) * mm});
            skLineSegment(sketch, "E158.0.0", {"start": v(225, 0) * mm, "end": v(250, 0) * mm});
            skLineSegment(sketch, "E158.0.1", {"start": v(250, 0) * mm, "end": v(250, 3) * mm});
            skLineSegment(sketch, "E158.0.2", {"start": v(250, 3) * mm, "end": v(225, 3) * mm});
            skLineSegment(sketch, "E158.0.3", {"start": v(225, 3) * mm, "end": v(225, 0) * mm});
            skLineSegment(sketch, "E159.0.1", {"start": v(275, 0) * mm, "end": v(275, 3) * mm});
            skLineSegment(sketch, "E159.0.3", {"start": v(250, 3) * mm, "end": v(250, 0) * mm});
            skLineSegment(sketch, "E160.0.0", {"start": v(275, 0) * mm, "end": v(300, 0) * mm});
            skLineSegment(sketch, "E160.0.1", {"start": v(300, 0) * mm, "end": v(300, 3) * mm});
            skLineSegment(sketch, "E160.0.2", {"start": v(300, 3) * mm, "end": v(275, 3) * mm});
            skLineSegment(sketch, "E160.0.3", {"start": v(275, 3) * mm, "end": v(275, 0) * mm});
            skLineSegment(sketch, "E161.0.1", {"start": v(325, 0) * mm, "end": v(325, 3) * mm});
            skLineSegment(sketch, "E161.0.3", {"start": v(300, 3) * mm, "end": v(300, 0) * mm});
            skLineSegment(sketch, "E162.0.0", {"start": v(325, 0) * mm, "end": v(350, 0) * mm});
            skLineSegment(sketch, "E162.0.2", {"start": v(350, 3) * mm, "end": v(325, 3) * mm});
            skLineSegment(sketch, "E162.0.3", {"start": v(325, 3) * mm, "end": v(325, 0) * mm});
            skLineSegment(sketch, "E163", {"start": v(0, 0) * mm, "end": v(0, -6) * mm});
            skLineSegment(sketch, "E164", {"start": v(0, -6) * mm, "end": v(347, -6) * mm});
            skLineSegment(sketch, "E165", {"start": v(350, -3) * mm, "end": v(350, 0) * mm});
            skLineSegment(sketch, "E166", {"start": v(0, 3) * mm, "end": v(0, 12) * mm, "construction": true});
            skLineSegment(sketch, "E167", {"start": v(0, 43) * mm, "end": v(6, 43) * mm});
            skLineSegment(sketch, "E168", {"start": v(350, 40) * mm, "end": v(350, 3) * mm});
            skLineSegment(sketch, "E169", {"start": v(0, 12) * mm, "end": v(150, 12) * mm, "construction": true});
            skPoint(sketch, "E169.endSnap0", {"position": v(350, 23) * mm});
            skLineSegment(sketch, "E170", {"start": v(117.48, 43) * mm, "end": v(117.48, 12) * mm, "construction": true});
            skLineSegment(sketch, "E171", {"start": v(330.2, 43) * mm, "end": v(330.2, 12) * mm, "construction": true});
            skLineSegment(sketch, "E172", {"start": v(125, 43) * mm, "end": v(149.1, 13.12) * mm});
            skLineSegment(sketch, "E173", {"start": v(297.49, 39.88) * mm, "end": v(275.9, 13.12) * mm});
            skLineSegment(sketch, "E174", {"start": v(0, 33) * mm, "end": v(8.55, 33) * mm, "construction": true});
            skCircle(sketch, "E175", {"center": v(117.48, 33) * mm, "radius": 2 * mm});
            skCircle(sketch, "E176", {"center": v(330.2, 33) * mm, "radius": 2 * mm});
            skLineSegment(sketch, "E177", {"start": v(6, 43) * mm, "end": v(6, 40) * mm});
            skLineSegment(sketch, "E178", {"start": v(6, 40) * mm, "end": v(11, 40) * mm});
            skLineSegment(sketch, "E179", {"start": v(11, 40) * mm, "end": v(11, 43) * mm});
            skLineSegment(sketch, "E180.trimOffspring", {"start": v(11, 43) * mm, "end": v(115, 43) * mm});
            skLineSegment(sketch, "E181", {"start": v(0, 33) * mm, "end": v(-3, 33) * mm});
            skLineSegment(sketch, "E182", {"start": v(-3, 33) * mm, "end": v(-3, 12) * mm});
            skLineSegment(sketch, "E183", {"start": v(-3, 12) * mm, "end": v(0, 12) * mm});
            skLineSegment(sketch, "E184", {"start": v(0, -6) * mm, "end": v(-4, -6) * mm});
            skLineSegment(sketch, "E185", {"start": v(-9, -1) * mm, "end": v(-9, 38) * mm});
            skLineSegment(sketch, "E186", {"start": v(-4, 43) * mm, "end": v(0, 43) * mm});
            skPoint(sketch, "E187.visualSharp", {"position": v(-9, 43) * mm});
            skArc(sketch, "E187.filletArc", {"start": v(-4, 43) * mm, "mid": v(-7.54, 41.54) * mm, "end": v(-9, 38) * mm});
            skPoint(sketch, "E188.visualSharp", {"position": v(-9, -6) * mm});
            skArc(sketch, "E188.filletArc", {"start": v(-9, -1) * mm, "mid": v(-7.54, -4.54) * mm, "end": v(-4, -6) * mm});
            skLineSegment(sketch, "E189", {"start": v(125, 43) * mm, "end": v(120, 43) * mm});
            skLineSegment(sketch, "E190", {"start": v(120, 43) * mm, "end": v(120, 40) * mm});
            skLineSegment(sketch, "E191", {"start": v(120, 40) * mm, "end": v(115, 40) * mm});
            skLineSegment(sketch, "E192", {"start": v(115, 40) * mm, "end": v(115, 43) * mm});
            skLineSegment(sketch, "E193.trimOffspring", {"start": v(120, 43) * mm, "end": v(125, 43) * mm});
            skLineSegment(sketch, "E194", {"start": v(344, 33) * mm, "end": v(344, 12) * mm});
            skLineSegment(sketch, "E195", {"start": v(344, 12) * mm, "end": v(341, 12) * mm});
            skLineSegment(sketch, "E196", {"start": v(341, 12) * mm, "end": v(341, 33) * mm});
            skLineSegment(sketch, "E197", {"start": v(341, 33) * mm, "end": v(344, 33) * mm});
            skPoint(sketch, "E198.start.orphan", {"position": v(350, 33) * mm});
            skPoint(sketch, "E199.orphan", {"position": v(350, 12) * mm});
            skLineSegment(sketch, "E200.trimOffspring", {"start": v(275, 12) * mm, "end": v(344, 12) * mm, "construction": true});
            skLineSegment(sketch, "E201", {"start": v(151.43, 12) * mm, "end": v(273.57, 12) * mm});
            skLineSegment(sketch, "E202.trimOffspring", {"start": v(0, 33) * mm, "end": v(0, 43) * mm, "construction": true});
            skLineSegment(sketch, "E203", {"start": v(0, 33) * mm, "end": v(0, 12) * mm});
            skLineSegment(sketch, "E204", {"start": v(349, 41) * mm, "end": v(299.82, 41) * mm});
            skPoint(sketch, "E205.start.orphan", {"position": v(300, 43) * mm});
            skPoint(sketch, "E206.orphan", {"position": v(310, 43) * mm});
            skPoint(sketch, "E207.orphan", {"position": v(350, 43) * mm});
            skLineSegment(sketch, "E208.bottom", {"start": v(10.55, 33) * mm, "end": v(36.55, 33) * mm});
            skLineSegment(sketch, "E208.top", {"start": v(10.55, 28) * mm, "end": v(36.55, 28) * mm});
            skLineSegment(sketch, "E208.left", {"start": v(8.55, 31) * mm, "end": v(8.55, 30) * mm});
            skLineSegment(sketch, "E208.right", {"start": v(38.55, 31) * mm, "end": v(38.55, 30) * mm});
            skLineSegment(sketch, "E209.trimOffspring", {"start": v(115.48, 33) * mm, "end": v(291.94, 33) * mm, "construction": true});
            skLineSegment(sketch, "E210.0.1.0", {"start": v(10.55, 23.8) * mm, "end": v(36.55, 23.8) * mm});
            skLineSegment(sketch, "E210.0.1.1", {"start": v(8.55, 21.8) * mm, "end": v(8.55, 20.8) * mm});
            skLineSegment(sketch, "E210.0.1.2", {"start": v(38.55, 21.8) * mm, "end": v(38.55, 20.8) * mm});
            skLineSegment(sketch, "E210.0.1.3", {"start": v(10.55, 18.8) * mm, "end": v(36.55, 18.8) * mm});
            skLineSegment(sketch, "E210.0.2.0", {"start": v(10.55, 14.6) * mm, "end": v(36.55, 14.6) * mm});
            skLineSegment(sketch, "E210.0.2.1", {"start": v(8.55, 12.6) * mm, "end": v(8.55, 11.6) * mm});
            skLineSegment(sketch, "E210.0.2.2", {"start": v(38.55, 12.6) * mm, "end": v(38.55, 11.6) * mm});
            skLineSegment(sketch, "E210.0.2.3", {"start": v(10.55, 9.6) * mm, "end": v(36.55, 9.6) * mm});
            skLineSegment(sketch, "E210.1.0.0", {"start": v(45.55, 33) * mm, "end": v(71.55, 33) * mm});
            skLineSegment(sketch, "E210.1.0.1", {"start": v(43.55, 31) * mm, "end": v(43.55, 30) * mm});
            skLineSegment(sketch, "E210.1.0.2", {"start": v(73.55, 31) * mm, "end": v(73.55, 30) * mm});
            skLineSegment(sketch, "E210.1.0.3", {"start": v(45.55, 28) * mm, "end": v(71.55, 28) * mm});
            skLineSegment(sketch, "E210.1.1.0", {"start": v(45.55, 23.8) * mm, "end": v(71.55, 23.8) * mm});
            skLineSegment(sketch, "E210.1.1.1", {"start": v(43.55, 21.8) * mm, "end": v(43.55, 20.8) * mm});
            skLineSegment(sketch, "E210.1.1.2", {"start": v(73.55, 21.8) * mm, "end": v(73.55, 20.8) * mm});
            skLineSegment(sketch, "E210.1.1.3", {"start": v(45.55, 18.8) * mm, "end": v(71.55, 18.8) * mm});
            skLineSegment(sketch, "E210.1.2.0", {"start": v(45.55, 14.6) * mm, "end": v(71.55, 14.6) * mm});
            skLineSegment(sketch, "E210.1.2.1", {"start": v(43.55, 12.6) * mm, "end": v(43.55, 11.6) * mm});
            skLineSegment(sketch, "E210.1.2.2", {"start": v(73.55, 12.6) * mm, "end": v(73.55, 11.6) * mm});
            skLineSegment(sketch, "E210.1.2.3", {"start": v(45.55, 9.6) * mm, "end": v(71.55, 9.6) * mm});
            skLineSegment(sketch, "E210.2.0.0", {"start": v(80.55, 33) * mm, "end": v(106.55, 33) * mm});
            skLineSegment(sketch, "E210.2.0.1", {"start": v(78.55, 31) * mm, "end": v(78.55, 30) * mm});
            skLineSegment(sketch, "E210.2.0.2", {"start": v(108.55, 31) * mm, "end": v(108.55, 30) * mm});
            skLineSegment(sketch, "E210.2.0.3", {"start": v(80.55, 28) * mm, "end": v(106.55, 28) * mm});
            skLineSegment(sketch, "E210.2.1.0", {"start": v(80.55, 23.8) * mm, "end": v(106.55, 23.8) * mm});
            skLineSegment(sketch, "E210.2.1.1", {"start": v(78.55, 21.8) * mm, "end": v(78.55, 20.8) * mm});
            skLineSegment(sketch, "E210.2.1.2", {"start": v(108.55, 21.8) * mm, "end": v(108.55, 20.8) * mm});
            skLineSegment(sketch, "E210.2.1.3", {"start": v(80.55, 18.8) * mm, "end": v(106.55, 18.8) * mm});
            skLineSegment(sketch, "E210.2.2.0", {"start": v(80.55, 14.6) * mm, "end": v(106.55, 14.6) * mm});
            skLineSegment(sketch, "E210.2.2.1", {"start": v(78.55, 12.6) * mm, "end": v(78.55, 11.6) * mm});
            skLineSegment(sketch, "E210.2.2.2", {"start": v(108.55, 12.6) * mm, "end": v(108.55, 11.6) * mm});
            skLineSegment(sketch, "E210.2.2.3", {"start": v(80.55, 9.6) * mm, "end": v(106.55, 9.6) * mm});
            skLineSegment(sketch, "E210.direction1", {"start": v(8.55, 28) * mm, "end": v(43.55, 28) * mm, "construction": true});
            skLineSegment(sketch, "E210.direction2", {"start": v(8.55, 28) * mm, "end": v(8.55, 18.8) * mm, "construction": true});
            skLineSegment(sketch, "E211.bottom", {"start": v(321.17, 33) * mm, "end": v(300.17, 33) * mm});
            skLineSegment(sketch, "E211.top", {"start": v(321.17, 28) * mm, "end": v(300.17, 28) * mm});
            skLineSegment(sketch, "E211.left", {"start": v(323.17, 31) * mm, "end": v(323.17, 30) * mm});
            skLineSegment(sketch, "E211.right", {"start": v(298.17, 31) * mm, "end": v(298.17, 30) * mm});
            skLineSegment(sketch, "E212.trimOffspring", {"start": v(323.17, 33) * mm, "end": v(344, 33) * mm, "construction": true});
            skLineSegment(sketch, "E213.0.1.0", {"start": v(321.17, 18.8) * mm, "end": v(300.17, 18.8) * mm});
            skLineSegment(sketch, "E213.0.1.1", {"start": v(298.17, 21.8) * mm, "end": v(298.17, 20.8) * mm});
            skLineSegment(sketch, "E213.0.1.2", {"start": v(323.17, 21.8) * mm, "end": v(323.17, 20.8) * mm});
            skLineSegment(sketch, "E213.0.1.3", {"start": v(321.17, 23.8) * mm, "end": v(300.17, 23.8) * mm});
            skLineSegment(sketch, "E213.0.2.0", {"start": v(321.17, 9.6) * mm, "end": v(300.17, 9.6) * mm});
            skLineSegment(sketch, "E213.0.2.1", {"start": v(298.17, 12.6) * mm, "end": v(298.17, 11.6) * mm});
            skLineSegment(sketch, "E213.0.2.2", {"start": v(323.17, 12.6) * mm, "end": v(323.17, 11.6) * mm});
            skLineSegment(sketch, "E213.0.2.3", {"start": v(321.17, 14.6) * mm, "end": v(300.17, 14.6) * mm});
            skLineSegment(sketch, "E213.direction1", {"start": v(298.17, 28) * mm, "end": v(323.17, 28) * mm, "construction": true});
            skLineSegment(sketch, "E213.direction2", {"start": v(298.17, 28) * mm, "end": v(298.17, 18.8) * mm, "construction": true});
            skPoint(sketch, "E214.visualSharp", {"position": v(350, 41) * mm});
            skArc(sketch, "E214.filletArc", {"start": v(350, 40) * mm, "mid": v(349.7, 40.7) * mm, "end": v(349, 41) * mm});
            skPoint(sketch, "E215.visualSharp", {"position": v(350, -6) * mm});
            skArc(sketch, "E215.filletArc", {"start": v(347, -6) * mm, "mid": v(349.12, -5.12) * mm, "end": v(350, -3) * mm});
            skPoint(sketch, "E216.visualSharp", {"position": v(298.39, 41) * mm});
            skArc(sketch, "E216.filletArc", {"start": v(299.82, 41) * mm, "mid": v(298.53, 40.7) * mm, "end": v(297.49, 39.88) * mm});
            skPoint(sketch, "E217.visualSharp", {"position": v(275, 12) * mm});
            skArc(sketch, "E217.filletArc", {"start": v(273.57, 12) * mm, "mid": v(274.86, 12.3) * mm, "end": v(275.9, 13.12) * mm});
            skPoint(sketch, "E218.visualSharp", {"position": v(150, 12) * mm});
            skArc(sketch, "E218.filletArc", {"start": v(149.1, 13.12) * mm, "mid": v(150.14, 12.3) * mm, "end": v(151.43, 12) * mm});
            skPoint(sketch, "E219.visualSharp", {"position": v(8.55, 33) * mm});
            skArc(sketch, "E219.filletArc", {"start": v(10.55, 33) * mm, "mid": v(9.14, 32.41) * mm, "end": v(8.55, 31) * mm});
            skPoint(sketch, "E220.visualSharp", {"position": v(8.55, 28) * mm});
            skArc(sketch, "E220.filletArc", {"start": v(8.55, 30) * mm, "mid": v(9.14, 28.59) * mm, "end": v(10.55, 28) * mm});
            skPoint(sketch, "E221.visualSharp", {"position": v(38.55, 33) * mm});
            skArc(sketch, "E221.filletArc", {"start": v(38.55, 31) * mm, "mid": v(37.97, 32.41) * mm, "end": v(36.55, 33) * mm});
            skPoint(sketch, "E222.visualSharp", {"position": v(38.55, 28) * mm});
            skArc(sketch, "E222.filletArc", {"start": v(36.55, 28) * mm, "mid": v(37.97, 28.59) * mm, "end": v(38.55, 30) * mm});
            skPoint(sketch, "E223.visualSharp", {"position": v(8.55, 23.8) * mm});
            skArc(sketch, "E223.filletArc", {"start": v(10.55, 23.8) * mm, "mid": v(9.14, 23.21) * mm, "end": v(8.55, 21.8) * mm});
            skPoint(sketch, "E224.visualSharp", {"position": v(8.55, 18.8) * mm});
            skArc(sketch, "E224.filletArc", {"start": v(8.55, 20.8) * mm, "mid": v(9.14, 19.39) * mm, "end": v(10.55, 18.8) * mm});
            skPoint(sketch, "E225.visualSharp", {"position": v(38.55, 23.8) * mm});
            skArc(sketch, "E225.filletArc", {"start": v(38.55, 21.8) * mm, "mid": v(37.97, 23.21) * mm, "end": v(36.55, 23.8) * mm});
            skPoint(sketch, "E226.visualSharp", {"position": v(38.55, 18.8) * mm});
            skArc(sketch, "E226.filletArc", {"start": v(36.55, 18.8) * mm, "mid": v(37.97, 19.39) * mm, "end": v(38.55, 20.8) * mm});
            skPoint(sketch, "E227.visualSharp", {"position": v(8.55, 14.6) * mm});
            skArc(sketch, "E227.filletArc", {"start": v(10.55, 14.6) * mm, "mid": v(9.14, 14.01) * mm, "end": v(8.55, 12.6) * mm});
            skPoint(sketch, "E228.visualSharp", {"position": v(8.55, 9.6) * mm});
            skArc(sketch, "E228.filletArc", {"start": v(8.55, 11.6) * mm, "mid": v(9.14, 10.19) * mm, "end": v(10.55, 9.6) * mm});
            skPoint(sketch, "E229.visualSharp", {"position": v(38.55, 14.6) * mm});
            skArc(sketch, "E229.filletArc", {"start": v(38.55, 12.6) * mm, "mid": v(37.97, 14.01) * mm, "end": v(36.55, 14.6) * mm});
            skPoint(sketch, "E230.visualSharp", {"position": v(38.55, 9.6) * mm});
            skArc(sketch, "E230.filletArc", {"start": v(36.55, 9.6) * mm, "mid": v(37.97, 10.19) * mm, "end": v(38.55, 11.6) * mm});
            skPoint(sketch, "E231.visualSharp", {"position": v(43.55, 33) * mm});
            skArc(sketch, "E231.filletArc", {"start": v(45.55, 33) * mm, "mid": v(44.14, 32.41) * mm, "end": v(43.55, 31) * mm});
            skPoint(sketch, "E232.visualSharp", {"position": v(43.55, 28) * mm});
            skArc(sketch, "E232.filletArc", {"start": v(43.55, 30) * mm, "mid": v(44.14, 28.59) * mm, "end": v(45.55, 28) * mm});
            skPoint(sketch, "E233.visualSharp", {"position": v(73.55, 33) * mm});
            skArc(sketch, "E233.filletArc", {"start": v(73.55, 31) * mm, "mid": v(72.97, 32.41) * mm, "end": v(71.55, 33) * mm});
            skPoint(sketch, "E234.visualSharp", {"position": v(73.55, 28) * mm});
            skArc(sketch, "E234.filletArc", {"start": v(71.55, 28) * mm, "mid": v(72.97, 28.59) * mm, "end": v(73.55, 30) * mm});
            skPoint(sketch, "E235.visualSharp", {"position": v(73.55, 23.8) * mm});
            skArc(sketch, "E235.filletArc", {"start": v(73.55, 21.8) * mm, "mid": v(72.97, 23.21) * mm, "end": v(71.55, 23.8) * mm});
            skPoint(sketch, "E236.visualSharp", {"position": v(73.55, 18.8) * mm});
            skArc(sketch, "E236.filletArc", {"start": v(71.55, 18.8) * mm, "mid": v(72.97, 19.39) * mm, "end": v(73.55, 20.8) * mm});
            skPoint(sketch, "E237.visualSharp", {"position": v(43.55, 23.8) * mm});
            skArc(sketch, "E237.filletArc", {"start": v(45.55, 23.8) * mm, "mid": v(44.14, 23.21) * mm, "end": v(43.55, 21.8) * mm});
            skPoint(sketch, "E238.visualSharp", {"position": v(43.55, 18.8) * mm});
            skArc(sketch, "E238.filletArc", {"start": v(43.55, 20.8) * mm, "mid": v(44.14, 19.39) * mm, "end": v(45.55, 18.8) * mm});
            skPoint(sketch, "E239.visualSharp", {"position": v(43.55, 14.6) * mm});
            skArc(sketch, "E239.filletArc", {"start": v(45.55, 14.6) * mm, "mid": v(44.14, 14.01) * mm, "end": v(43.55, 12.6) * mm});
            skPoint(sketch, "E240.visualSharp", {"position": v(73.55, 14.6) * mm});
            skArc(sketch, "E240.filletArc", {"start": v(73.55, 12.6) * mm, "mid": v(72.97, 14.01) * mm, "end": v(71.55, 14.6) * mm});
            skPoint(sketch, "E241.visualSharp", {"position": v(43.55, 9.6) * mm});
            skArc(sketch, "E241.filletArc", {"start": v(43.55, 11.6) * mm, "mid": v(44.14, 10.19) * mm, "end": v(45.55, 9.6) * mm});
            skPoint(sketch, "E242.visualSharp", {"position": v(73.55, 9.6) * mm});
            skArc(sketch, "E242.filletArc", {"start": v(71.55, 9.6) * mm, "mid": v(72.97, 10.19) * mm, "end": v(73.55, 11.6) * mm});
            skPoint(sketch, "E243.visualSharp", {"position": v(78.55, 9.6) * mm});
            skArc(sketch, "E243.filletArc", {"start": v(78.55, 11.6) * mm, "mid": v(79.14, 10.19) * mm, "end": v(80.55, 9.6) * mm});
            skPoint(sketch, "E244.visualSharp", {"position": v(78.55, 14.6) * mm});
            skArc(sketch, "E244.filletArc", {"start": v(80.55, 14.6) * mm, "mid": v(79.14, 14.01) * mm, "end": v(78.55, 12.6) * mm});
            skPoint(sketch, "E245.visualSharp", {"position": v(78.55, 18.8) * mm});
            skArc(sketch, "E245.filletArc", {"start": v(78.55, 20.8) * mm, "mid": v(79.14, 19.39) * mm, "end": v(80.55, 18.8) * mm});
            skPoint(sketch, "E246.visualSharp", {"position": v(78.55, 28) * mm});
            skArc(sketch, "E246.filletArc", {"start": v(78.55, 30) * mm, "mid": v(79.14, 28.59) * mm, "end": v(80.55, 28) * mm});
            skPoint(sketch, "E247.visualSharp", {"position": v(78.55, 33) * mm});
            skArc(sketch, "E247.filletArc", {"start": v(80.55, 33) * mm, "mid": v(79.14, 32.41) * mm, "end": v(78.55, 31) * mm});
            skPoint(sketch, "E248.visualSharp", {"position": v(78.55, 23.8) * mm});
            skArc(sketch, "E248.filletArc", {"start": v(80.55, 23.8) * mm, "mid": v(79.14, 23.21) * mm, "end": v(78.55, 21.8) * mm});
            skPoint(sketch, "E249.visualSharp", {"position": v(108.55, 33) * mm});
            skArc(sketch, "E249.filletArc", {"start": v(108.55, 31) * mm, "mid": v(107.97, 32.41) * mm, "end": v(106.55, 33) * mm});
            skPoint(sketch, "E250.visualSharp", {"position": v(108.55, 28) * mm});
            skArc(sketch, "E250.filletArc", {"start": v(106.55, 28) * mm, "mid": v(107.97, 28.59) * mm, "end": v(108.55, 30) * mm});
            skPoint(sketch, "E251.visualSharp", {"position": v(108.55, 18.8) * mm});
            skArc(sketch, "E251.filletArc", {"start": v(106.55, 18.8) * mm, "mid": v(107.97, 19.39) * mm, "end": v(108.55, 20.8) * mm});
            skPoint(sketch, "E252.visualSharp", {"position": v(108.55, 23.8) * mm});
            skArc(sketch, "E252.filletArc", {"start": v(108.55, 21.8) * mm, "mid": v(107.97, 23.21) * mm, "end": v(106.55, 23.8) * mm});
            skPoint(sketch, "E253.visualSharp", {"position": v(108.55, 14.6) * mm});
            skArc(sketch, "E253.filletArc", {"start": v(108.55, 12.6) * mm, "mid": v(107.97, 14.01) * mm, "end": v(106.55, 14.6) * mm});
            skPoint(sketch, "E254.visualSharp", {"position": v(108.55, 9.6) * mm});
            skArc(sketch, "E254.filletArc", {"start": v(106.55, 9.6) * mm, "mid": v(107.97, 10.19) * mm, "end": v(108.55, 11.6) * mm});
            skPoint(sketch, "E255.visualSharp", {"position": v(298.17, 33) * mm});
            skArc(sketch, "E255.filletArc", {"start": v(300.17, 33) * mm, "mid": v(298.75, 32.41) * mm, "end": v(298.17, 31) * mm});
            skPoint(sketch, "E256.visualSharp", {"position": v(298.17, 28) * mm});
            skArc(sketch, "E256.filletArc", {"start": v(298.17, 30) * mm, "mid": v(298.75, 28.59) * mm, "end": v(300.17, 28) * mm});
            skPoint(sketch, "E257.visualSharp", {"position": v(323.17, 33) * mm});
            skArc(sketch, "E257.filletArc", {"start": v(323.17, 31) * mm, "mid": v(322.58, 32.41) * mm, "end": v(321.17, 33) * mm});
            skPoint(sketch, "E258.visualSharp", {"position": v(323.17, 28) * mm});
            skArc(sketch, "E258.filletArc", {"start": v(321.17, 28) * mm, "mid": v(322.58, 28.59) * mm, "end": v(323.17, 30) * mm});
            skPoint(sketch, "E259.visualSharp", {"position": v(323.17, 18.8) * mm});
            skArc(sketch, "E259.filletArc", {"start": v(321.17, 18.8) * mm, "mid": v(322.58, 19.39) * mm, "end": v(323.17, 20.8) * mm});
            skPoint(sketch, "E260.visualSharp", {"position": v(298.17, 23.8) * mm});
            skArc(sketch, "E260.filletArc", {"start": v(300.17, 23.8) * mm, "mid": v(298.75, 23.21) * mm, "end": v(298.17, 21.8) * mm});
            skPoint(sketch, "E261.visualSharp", {"position": v(298.17, 18.8) * mm});
            skArc(sketch, "E261.filletArc", {"start": v(298.17, 20.8) * mm, "mid": v(298.75, 19.39) * mm, "end": v(300.17, 18.8) * mm});
            skPoint(sketch, "E262.visualSharp", {"position": v(323.17, 23.8) * mm});
            skArc(sketch, "E262.filletArc", {"start": v(323.17, 21.8) * mm, "mid": v(322.58, 23.21) * mm, "end": v(321.17, 23.8) * mm});
            skPoint(sketch, "E263.visualSharp", {"position": v(323.17, 14.6) * mm});
            skArc(sketch, "E263.filletArc", {"start": v(323.17, 12.6) * mm, "mid": v(322.58, 14.01) * mm, "end": v(321.17, 14.6) * mm});
            skPoint(sketch, "E264.visualSharp", {"position": v(298.17, 9.6) * mm});
            skArc(sketch, "E264.filletArc", {"start": v(298.17, 11.6) * mm, "mid": v(298.75, 10.19) * mm, "end": v(300.17, 9.6) * mm});
            skPoint(sketch, "E265.visualSharp", {"position": v(298.17, 14.6) * mm});
            skArc(sketch, "E265.filletArc", {"start": v(300.17, 14.6) * mm, "mid": v(298.75, 14.01) * mm, "end": v(298.17, 12.6) * mm});
            skPoint(sketch, "E266.visualSharp", {"position": v(323.17, 9.6) * mm});
            skArc(sketch, "E266.filletArc", {"start": v(321.17, 9.6) * mm, "mid": v(322.58, 10.19) * mm, "end": v(323.17, 11.6) * mm});
            skSolve(sketch);
        }
        {
            var Q0;
            Q0 = qSketchRegion(id + "F3", true);
            extrude(context, id + "F4", {"entities" : qUnion([Q0]), "oppositeDirection" : true, "depth" : getVariable(context, 'T'), "offsetDistance" : 25 * mm});
        }
        {
            var Q0;
            Q0=makeQuery(id+"F4.opExtrude","SWEPT_BODY",BODY,{"disambiguationData":[OSD([sQuery(id+"F3.wireOp",EDGE,"E150.0.0"),sQuery(id+"F3.wireOp",EDGE,"E150.0.2"),sQuery(id+"F3.wireOp",EDGE,"E150.0.3"),sQuery(id+"F3.wireOp",EDGE,"E151.0.3"),sQuery(id+"F3.wireOp",EDGE,"E152.0.0"),sQuery(id+"F3.wireOp",EDGE,"E152.0.2"),sQuery(id+"F3.wireOp",EDGE,"E152.0.3"),sQuery(id+"F3.wireOp",EDGE,"E153.0.3"),sQuery(id+"F3.wireOp",EDGE,"E154.0.0"),sQuery(id+"F3.wireOp",EDGE,"E154.0.2"),sQuery(id+"F3.wireOp",EDGE,"E154.0.3"),sQuery(id+"F3.wireOp",EDGE,"E155.0.3"),sQuery(id+"F3.wireOp",EDGE,"E156.0.0"),sQuery(id+"F3.wireOp",EDGE,"E156.0.2"),sQuery(id+"F3.wireOp",EDGE,"E156.0.3"),sQuery(id+"F3.wireOp",EDGE,"E157.0.3"),sQuery(id+"F3.wireOp",EDGE,"E158.0.0"),sQuery(id+"F3.wireOp",EDGE,"E158.0.2"),sQuery(id+"F3.wireOp",EDGE,"E158.0.3"),sQuery(id+"F3.wireOp",EDGE,"E159.0.3"),sQuery(id+"F3.wireOp",EDGE,"E160.0.0"),sQuery(id+"F3.wireOp",EDGE,"E160.0.2"),sQuery(id+"F3.wireOp",EDGE,"E160.0.3"),sQuery(id+"F3.wireOp",EDGE,"E161.0.3"),sQuery(id+"F3.wireOp",EDGE,"E162.0.0"),sQuery(id+"F3.wireOp",EDGE,"E162.0.2"),sQuery(id+"F3.wireOp",EDGE,"E162.0.3"),sQuery(id+"F3.wireOp",EDGE,"E164"),sQuery(id+"F3.wireOp",EDGE,"E165"),sQuery(id+"F3.wireOp",EDGE,"E168"),sQuery(id+"F3.wireOp",EDGE,"E175"),sQuery(id+"F3.wireOp",EDGE,"E176"),sQuery(id+"F3.wireOp",EDGE,"E167"),sQuery(id+"F3.wireOp",EDGE,"E177"),sQuery(id+"F3.wireOp",EDGE,"E178"),sQuery(id+"F3.wireOp",EDGE,"E179"),sQuery(id+"F3.wireOp",EDGE,"E180.trimOffspring"),sQuery(id+"F3.wireOp",EDGE,"E181"),sQuery(id+"F3.wireOp",EDGE,"E182"),sQuery(id+"F3.wireOp",EDGE,"E183"),sQuery(id+"F3.wireOp",EDGE,"E184"),sQuery(id+"F3.wireOp",EDGE,"E185"),sQuery(id+"F3.wireOp",EDGE,"E186"),sQuery(id+"F3.wireOp",EDGE,"E187.filletArc"),sQuery(id+"F3.wireOp",EDGE,"E188.filletArc"),sQuery(id+"F3.wireOp",EDGE,"E190"),sQuery(id+"F3.wireOp",EDGE,"E191"),sQuery(id+"F3.wireOp",EDGE,"E192"),sQuery(id+"F3.wireOp",EDGE,"E193.trimOffspring"),sQuery(id+"F3.wireOp",EDGE,"NmnGqFMR-fGWa-aiSj-OKOK-ov3D4ZIIKK7S"),sQuery(id+"F3.wireOp",EDGE,"6FDS4tfS-tKoe-5Cva-HmbA-YLjohjbfNsQH"),sQuery(id+"F3.wireOp",EDGE,"z7wya3qB-d1IK-HIlZ-XHP4-wtAe9my9GUas"),sQuery(id+"F3.wireOp",EDGE,"kandpN3H-GTba-ZFq8-1meL-0o3kHTYaYZ9C"),sQuery(id+"F3.wireOp",EDGE,"474270f3-c32e-4322-9c13-c46ebc483129.trimOffspring"),sQuery(id+"F3.wireOp",EDGE,"E194"),sQuery(id+"F3.wireOp",EDGE,"E195"),sQuery(id+"F3.wireOp",EDGE,"E196"),sQuery(id+"F3.wireOp",EDGE,"E197"),sQuery(id+"F3.wireOp",EDGE,"E203")])]});
            var Q1;
            Q1=qCreatedBy(makeId("Front.planeOp"),FACE);
            mirror(context, id + "F5", {"entities" : qUnion([Q0]), "mirrorPlane" : qUnion([Q1])});
        }
        {
            var Q0;
            Q0=makeQuery(id+"F2.opExtrude","SWEPT_FACE",FACE,{"disambiguationData":[OSD([sQuery(id+"F1.wireOp",EDGE,"E80"),sQuery(id+"F1.wireOp",EDGE,"E81.MirrorCS")])]});
            var sketch = newSketch(context, id + "F6", { "sketchPlane" : qUnion([Q0])});
            skLineSegment(sketch, "E267.0.1", {"start": v(10, 0) * mm, "end": v(10, 3) * mm});
            skLineSegment(sketch, "E267.0.2", {"start": v(10, 3) * mm, "end": v(-10, 3) * mm});
            skLineSegment(sketch, "E267.0.3", {"start": v(-10, 3) * mm, "end": v(-10, 0) * mm});
            skLineSegment(sketch, "E268.0.0", {"start": v(10, 0) * mm, "end": v(30.5, 0) * mm});
            skLineSegment(sketch, "E268.0.1", {"start": v(30.5, 0) * mm, "end": v(30.5, 3) * mm});
            skLineSegment(sketch, "E268.0.3", {"start": v(10, 3) * mm, "end": v(10, 0) * mm});
            skLineSegment(sketch, "E269.0.0", {"start": v(-30.5, 0) * mm, "end": v(-10, 0) * mm});
            skLineSegment(sketch, "E269.0.1", {"start": v(-10, 0) * mm, "end": v(-10, 3) * mm});
            skLineSegment(sketch, "E269.0.3", {"start": v(-30.5, 3) * mm, "end": v(-30.5, 0) * mm});
            skPoint(sketch, "E270.0", {"position": v(30.5, 43) * mm});
            skPoint(sketch, "E271.0", {"position": v(-30.5, 43) * mm});
            skLineSegment(sketch, "E272", {"start": v(-30.5, 43) * mm, "end": v(-10, 43) * mm});
            skLineSegment(sketch, "E273", {"start": v(-30.5, 43) * mm, "end": v(-30.5, 33) * mm});
            skLineSegment(sketch, "E274", {"start": v(30.5, 43) * mm, "end": v(30.5, 33) * mm});
            skLineSegment(sketch, "E275", {"start": v(33.5, 12) * mm, "end": v(30.5, 12) * mm});
            skLineSegment(sketch, "E276", {"start": v(33.5, 33) * mm, "end": v(30.5, 33) * mm});
            skLineSegment(sketch, "E277", {"start": v(30.5, 12) * mm, "end": v(30.5, 0) * mm});
            skLineSegment(sketch, "E278", {"start": v(-30.5, 33) * mm, "end": v(-33.5, 33) * mm});
            skLineSegment(sketch, "E279", {"start": v(-33.5, 12) * mm, "end": v(-30.5, 12) * mm});
            skLineSegment(sketch, "E280", {"start": v(-30.5, 12) * mm, "end": v(-30.5, 0) * mm});
            skLineSegment(sketch, "E281", {"start": v(-10, 43) * mm, "end": v(-10, 40) * mm});
            skLineSegment(sketch, "E282", {"start": v(-10, 40) * mm, "end": v(10, 40) * mm});
            skLineSegment(sketch, "E283", {"start": v(10, 40) * mm, "end": v(10, 43) * mm});
            skLineSegment(sketch, "E284.trimOffspring", {"start": v(10, 43) * mm, "end": v(30.5, 43) * mm});
            skLineSegment(sketch, "E285", {"start": v(0, 40) * mm, "end": v(0, 3) * mm, "construction": true});
            skLineSegment(sketch, "E286", {"start": v(30.53, 21.5) * mm, "end": v(-30.5, 21.5) * mm, "construction": true});
            skCircle(sketch, "E287", {"center": v(0.01, 21.5) * mm, "radius": 6.1 * mm});
            skLineSegment(sketch, "E288", {"start": v(-30.5, 33.08) * mm, "end": v(30.08, 33.08) * mm, "construction": true});
            skCircle(sketch, "E289", {"center": v(-11.58, 33.08) * mm, "radius": 1.65 * mm});
            skCircle(sketch, "E290.MirrorC", {"center": v(11.57, 33.08) * mm, "radius": 1.65 * mm});
            skCircle(sketch, "E291.MirrorC", {"center": v(-11.58, 9.92) * mm, "radius": 1.65 * mm});
            skCircle(sketch, "E292.MirrorC", {"center": v(11.57, 9.92) * mm, "radius": 1.65 * mm});
            skLineSegment(sketch, "E293.bottom", {"start": v(19.03, 25.59) * mm, "end": v(24.5, 25.59) * mm});
            skLineSegment(sketch, "E293.top", {"start": v(19.03, 17.41) * mm, "end": v(24.5, 17.41) * mm});
            skLineSegment(sketch, "E293.left", {"start": v(17.03, 23.59) * mm, "end": v(17.03, 19.41) * mm});
            skLineSegment(sketch, "E293.right", {"start": v(26.5, 23.59) * mm, "end": v(26.5, 19.41) * mm});
            skPoint(sketch, "E293.middle", {"position": v(21.76, 21.5) * mm});
            skPoint(sketch, "E294.visualSharp", {"position": v(17.03, 25.59) * mm});
            skArc(sketch, "E294.filletArc", {"start": v(19.03, 25.59) * mm, "mid": v(17.61, 25) * mm, "end": v(17.03, 23.59) * mm});
            skPoint(sketch, "E295.visualSharp", {"position": v(26.5, 25.59) * mm});
            skArc(sketch, "E295.filletArc", {"start": v(26.5, 23.59) * mm, "mid": v(25.91, 25) * mm, "end": v(24.5, 25.59) * mm});
            skPoint(sketch, "E296.visualSharp", {"position": v(26.5, 17.41) * mm});
            skArc(sketch, "E296.filletArc", {"start": v(24.5, 17.41) * mm, "mid": v(25.91, 18) * mm, "end": v(26.5, 19.41) * mm});
            skPoint(sketch, "E297.visualSharp", {"position": v(17.03, 17.41) * mm});
            skArc(sketch, "E297.filletArc", {"start": v(17.03, 19.41) * mm, "mid": v(17.61, 18) * mm, "end": v(19.03, 17.41) * mm});
            skLineSegment(sketch, "E298", {"start": v(-33.5, 33) * mm, "end": v(-41.5, 33) * mm});
            skLineSegment(sketch, "E299", {"start": v(-44.5, 30) * mm, "end": v(-44.5, 15) * mm});
            skLineSegment(sketch, "E300", {"start": v(-41.5, 12) * mm, "end": v(-33.5, 12) * mm});
            skLineSegment(sketch, "E301", {"start": v(33.5, 12) * mm, "end": v(41.5, 12) * mm});
            skLineSegment(sketch, "E302", {"start": v(44.5, 15) * mm, "end": v(44.5, 30.2) * mm});
            skLineSegment(sketch, "E303", {"start": v(41.7, 33) * mm, "end": v(33.5, 33) * mm});
            skPoint(sketch, "E304.visualSharp", {"position": v(-44.5, 33) * mm});
            skArc(sketch, "E304.filletArc", {"start": v(-41.5, 33) * mm, "mid": v(-43.62, 32.12) * mm, "end": v(-44.5, 30) * mm});
            skPoint(sketch, "E305.visualSharp", {"position": v(-44.5, 12) * mm});
            skArc(sketch, "E305.filletArc", {"start": v(-44.5, 15) * mm, "mid": v(-43.62, 12.88) * mm, "end": v(-41.5, 12) * mm});
            skPoint(sketch, "E306.visualSharp", {"position": v(44.5, 12) * mm});
            skArc(sketch, "E306.filletArc", {"start": v(41.5, 12) * mm, "mid": v(43.62, 12.88) * mm, "end": v(44.5, 15) * mm});
            skPoint(sketch, "E307.visualSharp", {"position": v(44.5, 33) * mm});
            skArc(sketch, "E307.filletArc", {"start": v(44.5, 30.2) * mm, "mid": v(43.68, 32.18) * mm, "end": v(41.7, 33) * mm});
            skSolve(sketch);
        }
        {
            var Q0;
            Q0=makeQuery(id+"F6.imprint","IMPRINT",FACE,{"disambiguationData":[TD([[makeQuery(id+"F6.imprint","IMPRINT",EDGE,{"derivedFrom":sQuery(id+"F6.wireOp",EDGE,"E267.0.2")}),1.0]])]});
            extrude(context, id + "F7", {"entities" : qUnion([Q0]), "oppositeDirection" : true, "depth" : getVariable(context, 'T'), "offsetDistance" : 25 * mm});
        }
        {
            var Q0;
            Q0=makeQuery(id+"F4.opExtrude","SWEPT_FACE",FACE,{"disambiguationData":[OSD([sQuery(id+"F3.wireOp",EDGE,"E196")])]});
            var sketch = newSketch(context, id + "F8", { "sketchPlane" : qUnion([Q0])});
            skLineSegment(sketch, "E308.0.0", {"start": v(33.5, 12) * mm, "end": v(33.5, 33) * mm});
            skLineSegment(sketch, "E308.0.1", {"start": v(33.5, 33) * mm, "end": v(30.5, 33) * mm});
            skLineSegment(sketch, "E308.0.3", {"start": v(30.5, 12) * mm, "end": v(33.5, 12) * mm});
            skPoint(sketch, "E309.0", {"position": v(30.5, 3) * mm});
            skLineSegment(sketch, "E310", {"start": v(30.5, 3) * mm, "end": v(30.5, 12) * mm});
            skLineSegment(sketch, "E311", {"start": v(0, 0) * mm, "end": v(10, 0) * mm});
            skLineSegment(sketch, "E312", {"start": v(10, 0) * mm, "end": v(10, 3) * mm});
            skLineSegment(sketch, "E313.trimOffspring", {"start": v(10, 3) * mm, "end": v(30.5, 3) * mm});
            skLineSegment(sketch, "E314", {"start": v(30.5, 12) * mm, "end": v(30.5, 3) * mm});
            skArc(sketch, "E315", {"start": v(0, 10) * mm, "mid": v(8.84, 13.66) * mm, "end": v(12.5, 22.5) * mm});
            skLineSegment(sketch, "E316.trimOffspring", {"start": v(27.5, 3) * mm, "end": v(30.5, 3) * mm});
            skPoint(sketch, "E317.visualSharp", {"position": v(12.5, 3) * mm});
            skPoint(sketch, "E318.0", {"position": v(30.5, 40) * mm});
            skLineSegment(sketch, "E319", {"start": v(30.5, 40) * mm, "end": v(27.5, 40) * mm});
            skLineSegment(sketch, "E320", {"start": v(12.5, 25) * mm, "end": v(12.5, 22.5) * mm});
            skPoint(sketch, "E321.visualSharp", {"position": v(12.5, 40) * mm});
            skArc(sketch, "E321.filletArc", {"start": v(27.5, 40) * mm, "mid": v(16.9, 35.6) * mm, "end": v(12.5, 25) * mm});
            skLineSegment(sketch, "E322", {"start": v(30.5, 33) * mm, "end": v(30.5, 40) * mm});
            skLineSegment(sketch, "E323", {"start": v(0, 0) * mm, "end": v(0, 10) * mm, "construction": true});
            skLineSegment(sketch, "E324.MirrorCS", {"start": v(-30.5, 3) * mm, "end": v(-30.5, 12) * mm});
            skPoint(sketch, "E325.MirrorP", {"position": v(-30.5, 3) * mm});
            skLineSegment(sketch, "E326.MirrorCS", {"start": v(-12.5, 25) * mm, "end": v(-12.5, 22.5) * mm});
            skLineSegment(sketch, "E327.MirrorCS", {"start": v(-10, 3) * mm, "end": v(-30.5, 3) * mm});
            skLineSegment(sketch, "E328.MirrorCS", {"start": v(-30.5, 40) * mm, "end": v(-27.5, 40) * mm});
            skLineSegment(sketch, "E329.MirrorCS", {"start": v(-27.5, 3) * mm, "end": v(-30.5, 3) * mm});
            skLineSegment(sketch, "E330.MirrorCS", {"start": v(0, 0) * mm, "end": v(-10, 0) * mm});
            skLineSegment(sketch, "E331.MirrorCS", {"start": v(-30.5, 33) * mm, "end": v(-30.5, 40) * mm});
            skLineSegment(sketch, "E332.MirrorCS", {"start": v(-30.5, 12) * mm, "end": v(-33.5, 12) * mm});
            skArc(sketch, "E333.MirrorCS", {"start": v(0, 10) * mm, "mid": v(-8.84, 13.66) * mm, "end": v(-12.5, 22.5) * mm});
            skPoint(sketch, "E334.MirrorP", {"position": v(-12.5, 3) * mm});
            skLineSegment(sketch, "E335.MirrorCS", {"start": v(-10, 0) * mm, "end": v(-10, 3) * mm});
            skPoint(sketch, "E336.MirrorP", {"position": v(-30.5, 40) * mm});
            skLineSegment(sketch, "E337.MirrorCS", {"start": v(-33.5, 12) * mm, "end": v(-33.5, 33) * mm});
            skArc(sketch, "E338.MirrorCS", {"start": v(-27.5, 40) * mm, "mid": v(-16.9, 35.6) * mm, "end": v(-12.5, 25) * mm});
            skPoint(sketch, "E339.MirrorP", {"position": v(-12.5, 40) * mm});
            skLineSegment(sketch, "E340.MirrorCS", {"start": v(-30.5, 12) * mm, "end": v(-30.5, 3) * mm});
            skLineSegment(sketch, "E341.MirrorCS", {"start": v(-33.5, 33) * mm, "end": v(-30.5, 33) * mm});
            skSolve(sketch);
        }
        {
            var Q0;
            Q0=makeQuery(id+"F7.opExtrude","SWEPT_FACE",FACE,{"disambiguationData":[OSD([sQuery(id+"F6.wireOp",EDGE,"E272")])]});
            var sketch = newSketch(context, id + "F9", { "sketchPlane" : qUnion([Q0])});
            skLineSegment(sketch, "E342.0.0", {"start": v(11, 33.5) * mm, "end": v(6, 33.5) * mm});
            skLineSegment(sketch, "E342.0.1", {"start": v(6, 33.5) * mm, "end": v(6, 30.5) * mm});
            skLineSegment(sketch, "E342.0.3", {"start": v(11, 30.5) * mm, "end": v(11, 33.5) * mm});
            skPoint(sketch, "E343.0", {"position": v(0, 30.5) * mm});
            skLineSegment(sketch, "E344.0.0", {"start": v(-3, 10) * mm, "end": v(-3, -10) * mm});
            skLineSegment(sketch, "E344.0.1", {"start": v(-3, -10) * mm, "end": v(0, -10) * mm});
            skLineSegment(sketch, "E344.0.3", {"start": v(0, 10) * mm, "end": v(-3, 10) * mm});
            skPoint(sketch, "E345.0", {"position": v(0, -30.5) * mm});
            skLineSegment(sketch, "E346.0.0", {"start": v(6, -33.5) * mm, "end": v(11, -33.5) * mm});
            skLineSegment(sketch, "E346.0.1", {"start": v(11, -33.5) * mm, "end": v(11, -30.5) * mm});
            skLineSegment(sketch, "E346.0.3", {"start": v(6, -30.5) * mm, "end": v(6, -33.5) * mm});
            skLineSegment(sketch, "E347.0.0", {"start": v(120, 33.5) * mm, "end": v(115, 33.5) * mm});
            skLineSegment(sketch, "E347.0.1", {"start": v(115, 33.5) * mm, "end": v(115, 30.5) * mm});
            skLineSegment(sketch, "E347.0.3", {"start": v(120, 30.5) * mm, "end": v(120, 33.5) * mm});
            skPoint(sketch, "E348.0", {"position": v(125, 30.5) * mm});
            skPoint(sketch, "E349.0", {"position": v(125, -30.5) * mm});
            skLineSegment(sketch, "E350.0.0", {"start": v(115, -33.5) * mm, "end": v(120, -33.5) * mm});
            skLineSegment(sketch, "E350.0.1", {"start": v(120, -33.5) * mm, "end": v(120, -30.5) * mm});
            skLineSegment(sketch, "E350.0.3", {"start": v(115, -30.5) * mm, "end": v(115, -33.5) * mm});
            skLineSegment(sketch, "E351", {"start": v(6, 30.5) * mm, "end": v(0, 30.5) * mm});
            skLineSegment(sketch, "E352", {"start": v(0, 30.5) * mm, "end": v(0, 10) * mm});
            skLineSegment(sketch, "E353", {"start": v(0, -10) * mm, "end": v(0, -30.5) * mm});
            skLineSegment(sketch, "E354", {"start": v(0, -30.5) * mm, "end": v(6, -30.5) * mm});
            skLineSegment(sketch, "E355", {"start": v(11, -30.5) * mm, "end": v(16, -30.5) * mm});
            skLineSegment(sketch, "E356", {"start": v(16, -30.5) * mm, "end": v(16, 30.5) * mm});
            skLineSegment(sketch, "E357", {"start": v(11, 30.5) * mm, "end": v(16, 30.5) * mm});
            skLineSegment(sketch, "E358", {"start": v(120, 30.5) * mm, "end": v(125, 30.5) * mm});
            skLineSegment(sketch, "E359", {"start": v(125, 30.5) * mm, "end": v(125, -30.5) * mm});
            skLineSegment(sketch, "E360", {"start": v(125, -30.5) * mm, "end": v(120, -30.5) * mm});
            skLineSegment(sketch, "E361", {"start": v(115, -30.5) * mm, "end": v(110, -30.5) * mm});
            skLineSegment(sketch, "E362", {"start": v(110, -30.5) * mm, "end": v(110, 30.5) * mm});
            skLineSegment(sketch, "E363", {"start": v(110, 30.5) * mm, "end": v(115, 30.5) * mm});
            skSolve(sketch);
        }
        {
            var Q0;
            Q0=makeQuery(id+"F9.imprint","IMPRINT",FACE,{"disambiguationData":[TD([[makeQuery(id+"F9.imprint","IMPRINT",EDGE,{"derivedFrom":sQuery(id+"F9.wireOp",EDGE,"E342.0.0")}),1.0]])]});
            var Q1;
            Q1=makeQuery(id+"F9.imprint","IMPRINT",FACE,{"disambiguationData":[TD([[makeQuery(id+"F9.imprint","IMPRINT",EDGE,{"derivedFrom":sQuery(id+"F9.wireOp",EDGE,"E347.0.0")}),1.0]])]});
            var Q2;
            Q2=makeQuery(id+"F9.imprint","IMPRINT",FACE,{"disambiguationData":[TD([[makeQuery(id+"F9.imprint","IMPRINT",EDGE,{"derivedFrom":sQuery(id+"F9.wireOp",EDGE,"6dfc50c9-3bee-4e17-86ff-d79a44eacc52.0.0")}),1.0]])]});
            extrude(context, id + "F10", {"entities" : qUnion([Q0, Q1, Q2]), "oppositeDirection" : true, "depth" : getVariable(context, 'T'), "offsetDistance" : 25 * mm});
        }
        {
            var Q0;
            Q0=makeQuery(id+"F8.imprint","IMPRINT",FACE,{"disambiguationData":[TD([[makeQuery(id+"F8.imprint","IMPRINT",EDGE,{"derivedFrom":sQuery(id+"F8.wireOp",EDGE,"E332.MirrorCS")}),-1.0]])]});
            var Q1;
            Q1=makeQuery(id+"F8.imprint","IMPRINT",FACE,{"disambiguationData":[TD([[makeQuery(id+"F8.imprint","IMPRINT",EDGE,{"derivedFrom":sQuery(id+"F8.wireOp",EDGE,"E308.0.0")}),1.0]])]});
            extrude(context, id + "F11", {"entities" : qUnion([Q0, Q1]), "depth" : getVariable(context, 'T'), "offsetDistance" : 25 * mm});
        }
    });
